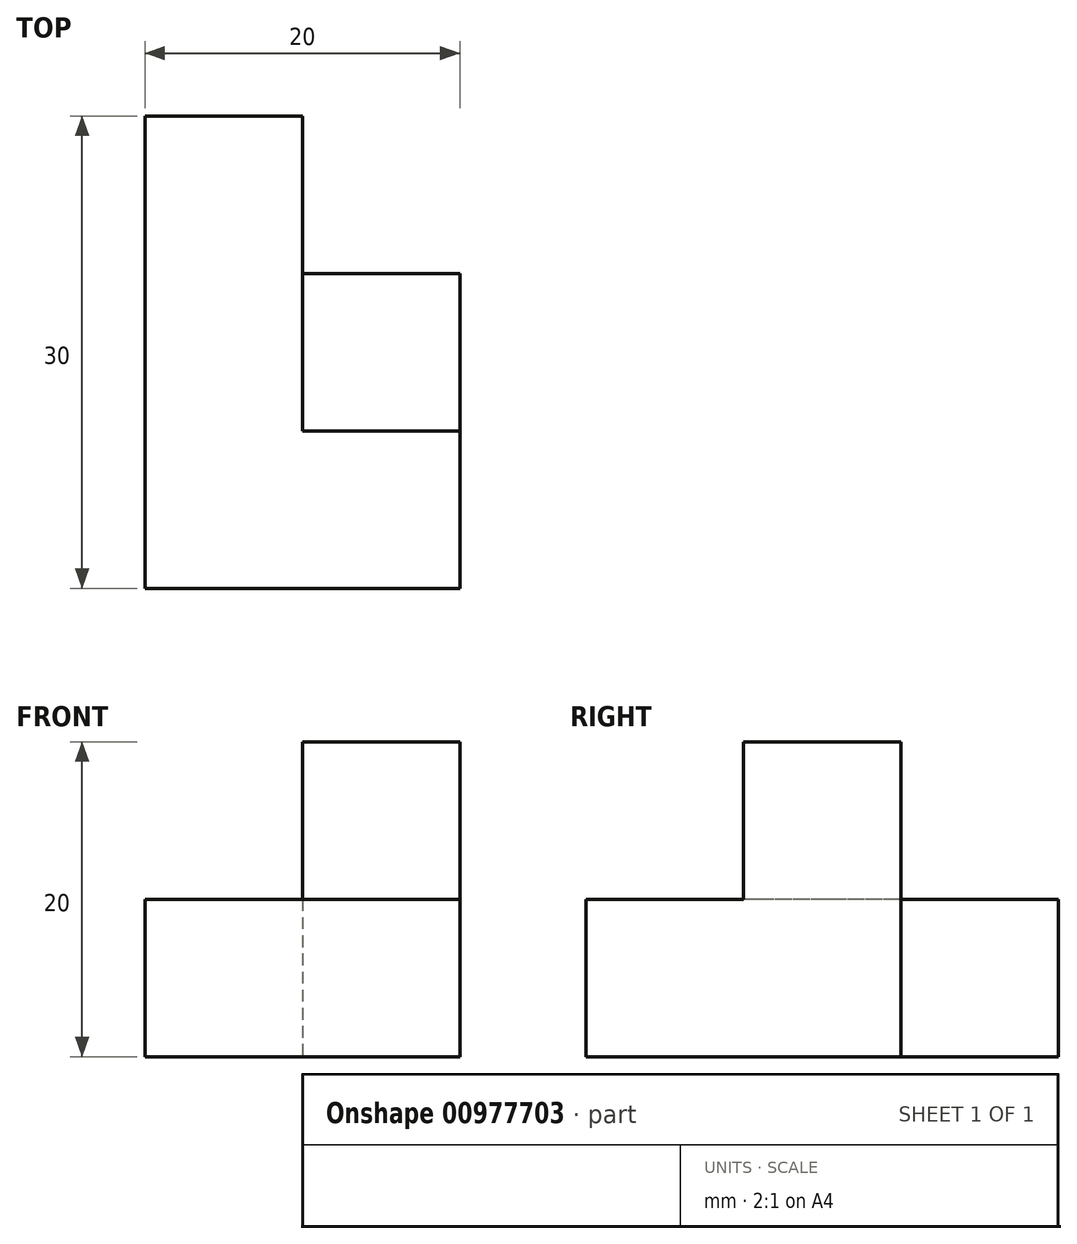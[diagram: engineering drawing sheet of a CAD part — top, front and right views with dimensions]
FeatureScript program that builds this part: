
annotation { "Feature Type Name" : "Feature", "Feature Type Description" : "" }
export const myFeature = defineFeature(function(context is Context, id is Id, definition is map)
    precondition{}
    {
        {
            var Q0;
            Q0=qCreatedBy(makeId("Top.planeOp"),FACE);
            var sketch = newSketch(context, id + "F0", { "sketchPlane" : qUnion([Q0])});
            skLineSegment(sketch, "E0", {"start": v(-27.57, -2.32) * mm, "end": v(-27.57, -32.32) * mm});
            skLineSegment(sketch, "E1", {"start": v(-27.57, -32.32) * mm, "end": v(-7.57, -32.32) * mm});
            skLineSegment(sketch, "E2", {"start": v(-7.57, -32.32) * mm, "end": v(-7.57, -12.32) * mm});
            skLineSegment(sketch, "E3", {"start": v(-7.57, -12.32) * mm, "end": v(-17.57, -12.32) * mm});
            skLineSegment(sketch, "E4", {"start": v(-17.57, -12.32) * mm, "end": v(-17.57, -2.32) * mm});
            skLineSegment(sketch, "E5", {"start": v(-17.57, -2.32) * mm, "end": v(-25.73, -2.32) * mm});
            skLineSegment(sketch, "E6", {"start": v(-25.73, -2.32) * mm, "end": v(-27.57, -2.32) * mm});
            skSolve(sketch);
        }
        {
            var Q0;
            Q0=makeQuery(id+"F0.imprint","IMPRINT",FACE,{"disambiguationData":[TD([[makeQuery(id+"F0.imprint","IMPRINT",EDGE,{"derivedFrom":sQuery(id+"F0.wireOp",EDGE,"E0")}),1.0]])]});
            extrude(context, id + "F1", {"entities" : qUnion([Q0]), "depth" : 10 * mm, "offsetDistance" : 25 * mm});
        }
        {
            var Q0;
            Q0=makeQuery(id+"F1.opExtrude","CAP_FACE",FACE,{"disambiguationData":[OSD([sQuery(id+"F0.wireOp",EDGE,"E0"),sQuery(id+"F0.wireOp",EDGE,"E1"),sQuery(id+"F0.wireOp",EDGE,"E2"),sQuery(id+"F0.wireOp",EDGE,"E3"),sQuery(id+"F0.wireOp",EDGE,"E4"),sQuery(id+"F0.wireOp",EDGE,"E5"),sQuery(id+"F0.wireOp",EDGE,"E6")])],"isStart":false});
            var sketch = newSketch(context, id + "F2", { "sketchPlane" : qUnion([Q0])});
            skLineSegment(sketch, "E7.bottom", {"start": v(-17.57, -12.32) * mm, "end": v(-7.57, -12.32) * mm});
            skLineSegment(sketch, "E7.top", {"start": v(-17.57, -22.32) * mm, "end": v(-7.57, -22.32) * mm});
            skLineSegment(sketch, "E7.left", {"start": v(-17.57, -12.32) * mm, "end": v(-17.57, -22.32) * mm});
            skLineSegment(sketch, "E7.right", {"start": v(-7.57, -12.32) * mm, "end": v(-7.57, -22.32) * mm});
            skSolve(sketch);
        }
        {
            var Q0;
            Q0=makeQuery(id+"F2.imprint","IMPRINT",FACE,{"disambiguationData":[TD([[makeQuery(id+"F2.imprint","IMPRINT",EDGE,{"derivedFrom":sQuery(id+"F2.wireOp",EDGE,"E7.bottom")}),1.0]])]});
            extrude(context, id + "F3", {"entities" : qUnion([Q0]), "operationType" : NewBodyOperationType.ADD, "depth" : 10 * mm, "offsetDistance" : 25 * mm});
        }
    });
